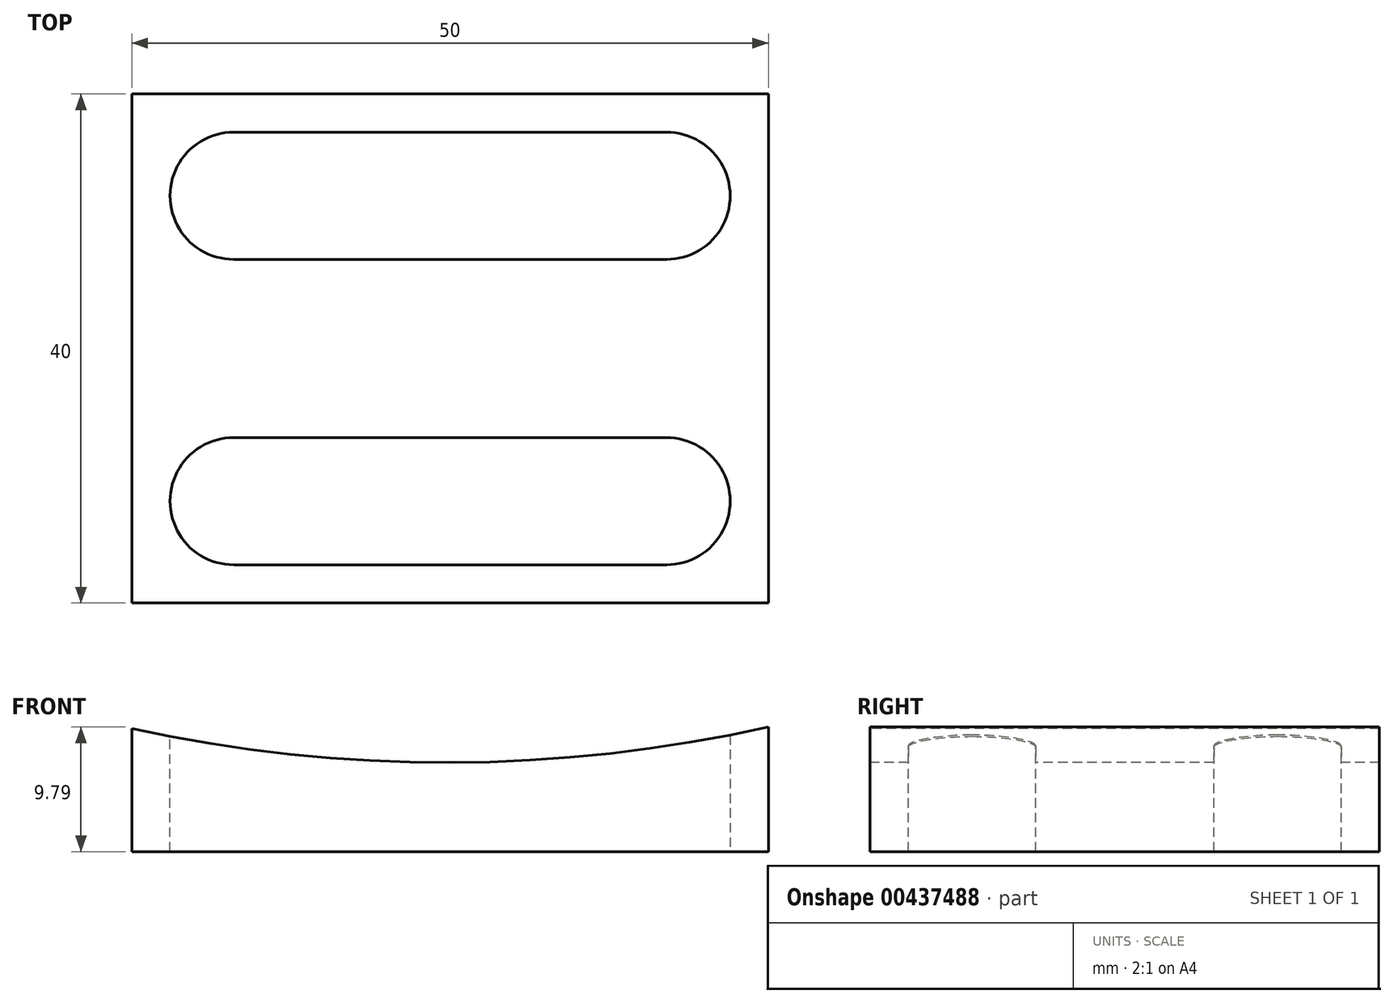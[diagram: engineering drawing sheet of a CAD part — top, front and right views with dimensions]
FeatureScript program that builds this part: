
annotation { "Feature Type Name" : "Feature", "Feature Type Description" : "" }
export const myFeature = defineFeature(function(context is Context, id is Id, definition is map)
    precondition{}
    {
        {
            var Q0;
            Q0=qCreatedBy(makeId("Top.planeOp"),FACE);
            var sketch = newSketch(context, id + "F0", { "sketchPlane" : qUnion([Q0])});
            skLineSegment(sketch, "E0.bottom", {"start": v(-25, -20) * mm, "end": v(25, -20) * mm});
            skLineSegment(sketch, "E0.top", {"start": v(-25, 20) * mm, "end": v(25, 20) * mm});
            skLineSegment(sketch, "E0.left", {"start": v(-25, -20) * mm, "end": v(-25, 20) * mm});
            skLineSegment(sketch, "E0.right", {"start": v(25, -20) * mm, "end": v(25, 20) * mm});
            skPoint(sketch, "E0.middle", {"position": v(0, 0) * mm});
            skSolve(sketch);
        }
        {
            var Q0;
            Q0=makeQuery(id+"F0.imprint","IMPRINT",FACE,{"disambiguationData":[TD([[makeQuery(id+"F0.imprint","IMPRINT",EDGE,{"derivedFrom":sQuery(id+"F0.wireOp",EDGE,"E0.bottom")}),1.0]])]});
            extrude(context, id + "F1", {"entities" : qUnion([Q0]), "depth" : 10 * mm, "offsetDistance" : 25 * mm});
        }
        {
            var Q0;
            Q0=makeQuery(id+"F1.opExtrude","SWEPT_FACE",FACE,{"disambiguationData":[OSD([sQuery(id+"F0.wireOp",EDGE,"E0.bottom")])]});
            var sketch = newSketch(context, id + "F2", { "sketchPlane" : qUnion([Q0])});
            skLineSegment(sketch, "E1", {"start": v(-39.61, 7) * mm, "end": v(41.52, 7) * mm, "construction": true});
            skLineSegment(sketch, "E2", {"start": v(0, -9.55) * mm, "end": v(0, 37.04) * mm, "construction": true});
            skCircle(sketch, "E3", {"center": v(-0.27, 123) * mm, "radius": 116 * mm});
            skPoint(sketch, "E3.first.point", {"position": v(0, 7) * mm});
            skPoint(sketch, "E3.second.point", {"position": v(0, 239) * mm});
            skPoint(sketch, "E3.second.point.positionSnap0", {"position": v(0, 10) * mm});
            skPoint(sketch, "E3.third.point", {"position": v(106.48, 77.6) * mm});
            skSolve(sketch);
        }
        {
            var Q0;
            {var subQ1=sQuery(id+"F0.wireOp",EDGE,"E0.bottom");var subQ6=makeQuery(id+"F1.opExtrude","CAP_EDGE",EDGE,{"disambiguationData":[OSD([subQ1])],"isStart":false});Q0=makeQuery(id+"F2.imprint","IMPRINT",FACE,{"disambiguationData":[TD([[makeQuery(id+"F2.imprint","IMPRINT",EDGE,{"derivedFrom":subQ6}),-1.0]])]});}
            extrude(context, id + "F3", {"entities" : qUnion([Q0]), "operationType" : NewBodyOperationType.REMOVE, "oppositeDirection" : true, "depth" : 40 * mm, "offsetDistance" : 25 * mm});
        }
        {
            var Q0;
            Q0=qCreatedBy(makeId("Top.planeOp"),FACE);
            cPlane(context, id + "F4", {"entities" : qUnion([Q0]), "cplaneType" : CPlaneType.OFFSET, "offset" : 10 * mm, "width" : 150 * mm, "height" : 150 * mm});
        }
        {
            var Q0;
            Q0=qCreatedBy(id+"F4.planeOp",FACE);
            var sketch = newSketch(context, id + "F5", { "sketchPlane" : qUnion([Q0])});
            skLineSegment(sketch, "E4.bottom", {"start": v(-22, 17) * mm, "end": v(22, 17) * mm});
            skLineSegment(sketch, "E4.top", {"start": v(-22, 7) * mm, "end": v(22, 7) * mm});
            skLineSegment(sketch, "E4.left", {"start": v(-22, 17) * mm, "end": v(-22, 7) * mm});
            skLineSegment(sketch, "E4.right", {"start": v(22, 17) * mm, "end": v(22, 7) * mm});
            skPoint(sketch, "E5.oppositeSnap0", {"position": v(22, 12) * mm});
            skLineSegment(sketch, "E5.bottom", {"start": v(-22, -7) * mm, "end": v(22, -7) * mm});
            skLineSegment(sketch, "E5.top", {"start": v(-22, -17) * mm, "end": v(22, -17) * mm});
            skLineSegment(sketch, "E5.left", {"start": v(-22, -7) * mm, "end": v(-22, -17) * mm});
            skLineSegment(sketch, "E5.right", {"start": v(22, -7) * mm, "end": v(22, -17) * mm});
            skSolve(sketch);
        }
        {
            var Q0;
            Q0 = qSketchRegion(id + "F5", true);
            extrude(context, id + "F6", {"entities" : qUnion([Q0]), "operationType" : NewBodyOperationType.REMOVE, "oppositeDirection" : true, "depth" : 18 * mm, "offsetDistance" : 25 * mm});
        }
        {
            var Q0;
            Q0=makeQuery(id+"F6.boolean.opBoolean","COPY",EDGE,{"derivedFrom":makeQuery(id+"F6.opExtrude","SWEPT_EDGE",EDGE,{"disambiguationData":[OSD([sQuery(id+"F5.wireOp",EDGE,"E4.bottom"),sQuery(id+"F5.wireOp",EDGE,"E4.left")])]})});
            var Q1;
            Q1=makeQuery(id+"F6.boolean.opBoolean","COPY",EDGE,{"derivedFrom":makeQuery(id+"F6.opExtrude","SWEPT_EDGE",EDGE,{"disambiguationData":[OSD([sQuery(id+"F5.wireOp",EDGE,"E4.bottom"),sQuery(id+"F5.wireOp",EDGE,"E4.right")])]})});
            var Q2;
            Q2=makeQuery(id+"F6.boolean.opBoolean","COPY",EDGE,{"derivedFrom":makeQuery(id+"F6.opExtrude","SWEPT_EDGE",EDGE,{"disambiguationData":[OSD([sQuery(id+"F5.wireOp",EDGE,"E5.bottom"),sQuery(id+"F5.wireOp",EDGE,"E5.left")])]})});
            var Q3;
            Q3=makeQuery(id+"F6.boolean.opBoolean","COPY",EDGE,{"derivedFrom":makeQuery(id+"F6.opExtrude","SWEPT_EDGE",EDGE,{"disambiguationData":[OSD([sQuery(id+"F5.wireOp",EDGE,"E5.bottom"),sQuery(id+"F5.wireOp",EDGE,"E5.right")])]})});
            var Q4;
            Q4=makeQuery(id+"F6.boolean.opBoolean","COPY",EDGE,{"derivedFrom":makeQuery(id+"F6.opExtrude","SWEPT_EDGE",EDGE,{"disambiguationData":[OSD([sQuery(id+"F5.wireOp",EDGE,"E5.top"),sQuery(id+"F5.wireOp",EDGE,"E5.left")])]})});
            var Q5;
            Q5=makeQuery(id+"F6.boolean.opBoolean","COPY",EDGE,{"derivedFrom":makeQuery(id+"F6.opExtrude","SWEPT_EDGE",EDGE,{"disambiguationData":[OSD([sQuery(id+"F5.wireOp",EDGE,"E5.top"),sQuery(id+"F5.wireOp",EDGE,"E5.right")])]})});
            var Q6;
            Q6=makeQuery(id+"F6.boolean.opBoolean","COPY",EDGE,{"derivedFrom":makeQuery(id+"F6.opExtrude","SWEPT_EDGE",EDGE,{"disambiguationData":[OSD([sQuery(id+"F5.wireOp",EDGE,"E4.top"),sQuery(id+"F5.wireOp",EDGE,"E4.right")])]})});
            var Q7;
            Q7=makeQuery(id+"F6.boolean.opBoolean","COPY",EDGE,{"derivedFrom":makeQuery(id+"F6.opExtrude","SWEPT_EDGE",EDGE,{"disambiguationData":[OSD([sQuery(id+"F5.wireOp",EDGE,"E4.top"),sQuery(id+"F5.wireOp",EDGE,"E4.left")])]})});
            fillet(context, id + "F7", {"entities" : qUnion([Q0, Q1, Q2, Q3, Q4, Q5, Q6, Q7]), "radius" : 5 * mm, "tangentPropagation" : true, "allowEdgeOverflow" : false});
        }
    });
